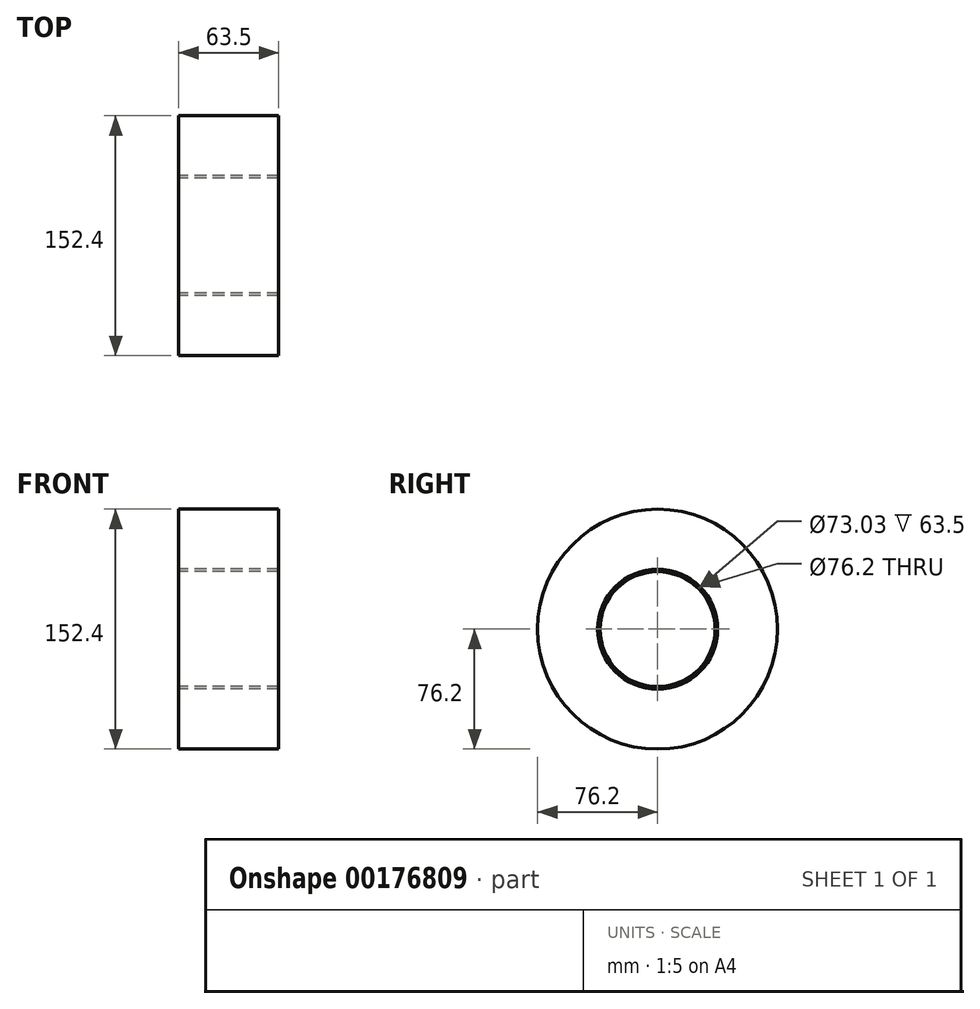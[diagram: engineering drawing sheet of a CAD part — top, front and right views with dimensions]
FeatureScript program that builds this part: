
annotation { "Feature Type Name" : "Feature", "Feature Type Description" : "" }
export const myFeature = defineFeature(function(context is Context, id is Id, definition is map)
    precondition{}
    {
        {
            var Q0;
            Q0=qCreatedBy(makeId("Right.planeOp"),FACE);
            var sketch = newSketch(context, id + "F0", { "sketchPlane" : qUnion([Q0])});
            skCircle(sketch, "E0", {"center": v(0, 0) * mm, "radius": 38.1 * mm});
            skCircle(sketch, "E1", {"center": v(0, 0) * mm, "radius": 76.2 * mm});
            skCircle(sketch, "E2", {"center": v(0, 0) * mm, "radius": 36.51 * mm});
            skSolve(sketch);
        }
        {
            var Q0;
            Q0=makeQuery(id+"F0.imprint","IMPRINT",FACE,{"disambiguationData":[TD([[makeQuery(id+"F0.imprint","IMPRINT",EDGE,{"derivedFrom":sQuery(id+"F0.wireOp",EDGE,"E0")}),-1.0]])]});
            extrude(context, id + "F1", {"entities" : qUnion([Q0]), "depth" : 63.5 * mm});
        }
        {
            var Q0;
            Q0=makeQuery(id+"F0.imprint","IMPRINT",FACE,{"disambiguationData":[TD([[makeQuery(id+"F0.imprint","IMPRINT",EDGE,{"derivedFrom":sQuery(id+"F0.wireOp",EDGE,"E0")}),1.0]])]});
            extrude(context, id + "F2", {"entities" : qUnion([Q0]), "depth" : 63.5 * mm});
        }
    });
